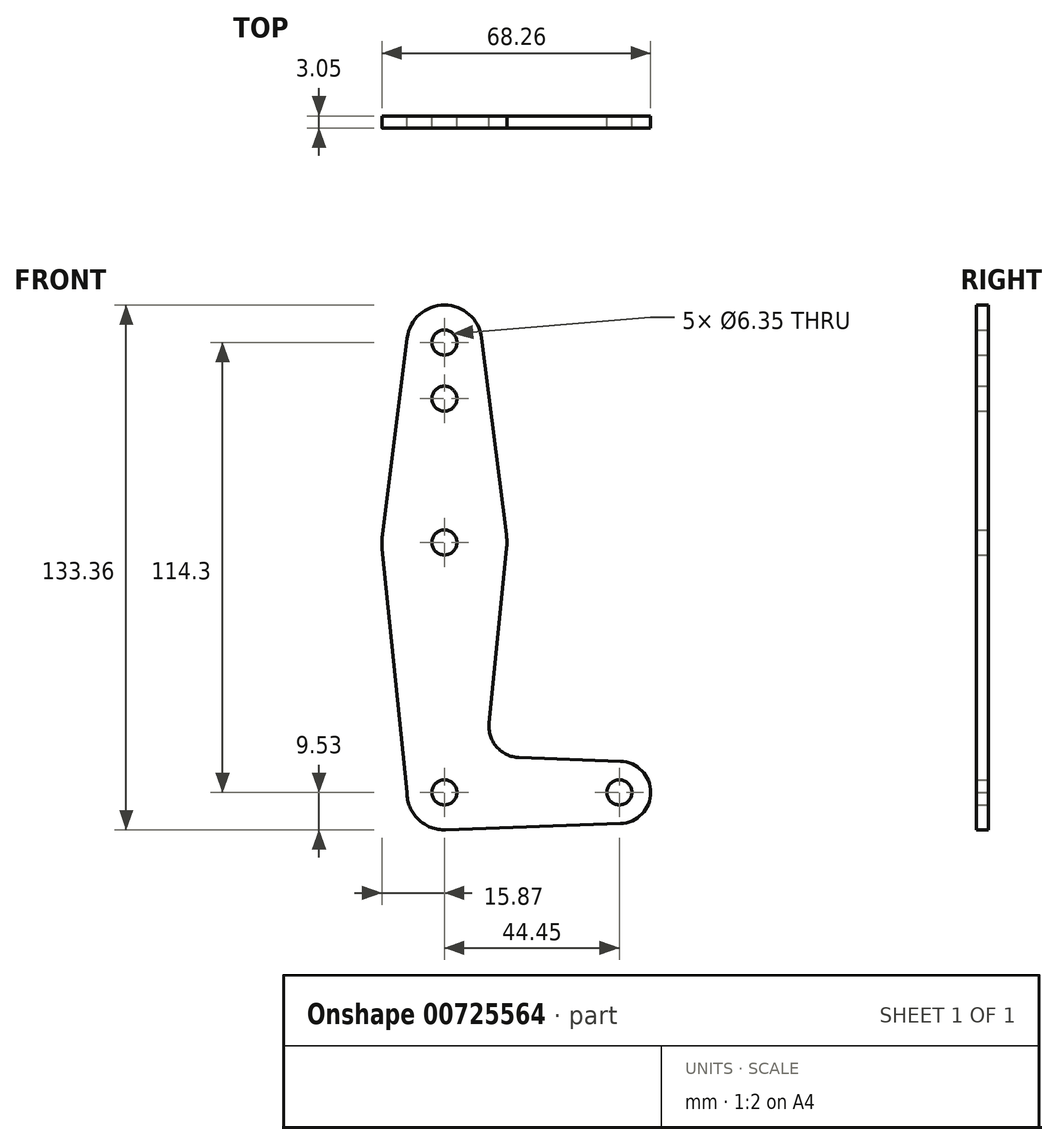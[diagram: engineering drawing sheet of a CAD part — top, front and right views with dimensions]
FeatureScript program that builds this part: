
annotation { "Feature Type Name" : "Feature", "Feature Type Description" : "" }
export const myFeature = defineFeature(function(context is Context, id is Id, definition is map)
    precondition{}
    {
        {
            var Q0;
            Q0=qCreatedBy(makeId("Front.planeOp"),FACE);
            var sketch = newSketch(context, id + "F0", { "sketchPlane" : qUnion([Q0])});
            skCircle(sketch, "E0", {"center": v(0, 0) * mm, "radius": 9.53 * mm});
            skCircle(sketch, "E1", {"center": v(0, 114.3) * mm, "radius": 9.53 * mm});
            skLineSegment(sketch, "E2", {"start": v(0, 0) * mm, "end": v(0, 0) * mm});
            skLineSegment(sketch, "E3", {"start": v(0, 0) * mm, "end": v(44.45, 0) * mm, "construction": true});
            skCircle(sketch, "E4", {"center": v(44.45, 0) * mm, "radius": 7.94 * mm});
            skCircle(sketch, "E5", {"center": v(0, 63.5) * mm, "radius": 15.88 * mm});
            skLineSegment(sketch, "E6", {"start": v(-9.45, 115.5) * mm, "end": v(-15.75, 65.48) * mm});
            skLineSegment(sketch, "E7", {"start": v(0.34, -9.52) * mm, "end": v(44.73, -7.93) * mm});
            skLineSegment(sketch, "E8", {"start": v(18.97, 8.86) * mm, "end": v(44.73, 7.93) * mm});
            skLineSegment(sketch, "E9", {"start": v(9.45, 115.5) * mm, "end": v(15.75, 65.48) * mm});
            skLineSegment(sketch, "E10", {"start": v(15.8, 61.91) * mm, "end": v(11.34, 17.6) * mm});
            skCircle(sketch, "E11", {"center": v(0, 114.3) * mm, "radius": 3.18 * mm});
            skCircle(sketch, "E12", {"center": v(0, 100.03) * mm, "radius": 3.18 * mm});
            skCircle(sketch, "E13", {"center": v(0, 63.5) * mm, "radius": 3.18 * mm});
            skCircle(sketch, "E14", {"center": v(0, 0) * mm, "radius": 3.18 * mm});
            skCircle(sketch, "E15", {"center": v(44.45, 0) * mm, "radius": 3.18 * mm});
            skArc(sketch, "E16.filletArc", {"start": v(11.34, 17.6) * mm, "mid": v(13.26, 11.57) * mm, "end": v(18.97, 8.86) * mm});
            skLineSegment(sketch, "E17", {"start": v(0, 114.3) * mm, "end": v(0, 0) * mm, "construction": true});
            skLineSegment(sketch, "E18", {"start": v(-15.8, 61.9) * mm, "end": v(-9.52, 0) * mm});
            skSolve(sketch);
        }
        {
            var Q0;
            {var subQ0=sQuery(id+"F0.wireOp",EDGE,"E6");Q0=makeQuery(id+"F0.imprint","IMPRINT",FACE,{"disambiguationData":[TD([[makeQuery(id+"F0.imprint","IMPRINT",EDGE,{"derivedFrom":subQ0}),1.0]])]});}
            var Q1;
            Q1=makeQuery(id+"F0.imprint","IMPRINT",FACE,{"disambiguationData":[TD([[makeQuery(id+"F0.imprint","IMPRINT",EDGE,{"derivedFrom":sQuery(id+"F0.wireOp",EDGE,"E11")}),-1.0]])]});
            var Q2;
            Q2=makeQuery(id+"F0.imprint","IMPRINT",FACE,{"disambiguationData":[TD([[makeQuery(id+"F0.imprint","IMPRINT",EDGE,{"derivedFrom":sQuery(id+"F0.wireOp",EDGE,"E13")}),-1.0]])]});
            var Q3;
            {var subQ3=sQuery(id+"F0.wireOp",EDGE,"E7");Q3=makeQuery(id+"F0.imprint","IMPRINT",FACE,{"disambiguationData":[TD([[makeQuery(id+"F0.imprint","IMPRINT",EDGE,{"derivedFrom":subQ3}),1.0]])]});}
            var Q4;
            Q4=makeQuery(id+"F0.imprint","IMPRINT",FACE,{"disambiguationData":[TD([[makeQuery(id+"F0.imprint","IMPRINT",EDGE,{"derivedFrom":sQuery(id+"F0.wireOp",EDGE,"E14")}),-1.0]])]});
            var Q5;
            Q5=makeQuery(id+"F0.imprint","IMPRINT",FACE,{"disambiguationData":[TD([[makeQuery(id+"F0.imprint","IMPRINT",EDGE,{"derivedFrom":sQuery(id+"F0.wireOp",EDGE,"E15")}),-1.0]])]});
            extrude(context, id + "F1", {"entities" : qUnion([Q0, Q1, Q2, Q3, Q4, Q5]), "depth" : 3.05 * mm, "offsetDistance" : 25.4 * mm});
        }
    });
